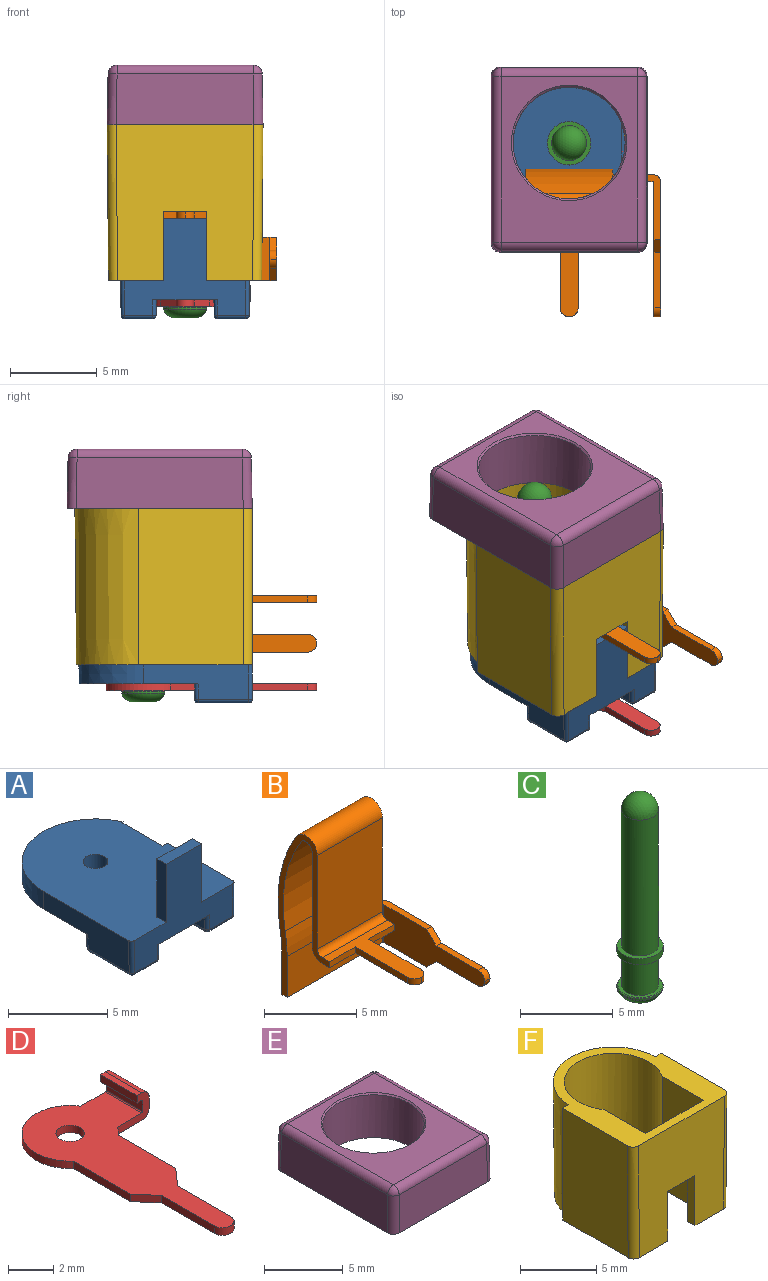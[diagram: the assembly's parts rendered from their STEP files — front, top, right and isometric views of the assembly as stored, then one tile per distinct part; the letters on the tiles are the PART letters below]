
ASSEMBLY  parts=6 mates=5
PART A: 44 faces, bbox 7.4x10x5.8 mm
  f0: cylinder r=0.62mm len=1.25mm, axis (0,0,1), area 4.3mm2, adj f1,f2
  f1: plane 9.98x7.4mm, normal (0,0,-1), area 52.3mm2, adj f0,f3,f4,f5,f6,f7,f8,f9
  f2: plane 9.99x7.41mm, normal (0,0,1), area 64.3mm2, adj f0,f3,f4,f5,f6,f7,f8,f9
  f3: plane 4.63x1.99mm, normal (1,0,-0.01), area 7.7mm2, adj f1,f2,f9,f34,f39,f40
  f4: plane 7.01x5.58mm, normal (0,-1,0), area 19.5mm2, adj f1,f2,f10,f11,f12,f25,f28,f31
  f5: plane 6.08x1.99mm, normal (-1,0,-0.01), area 9.3mm2, adj f1,f2,f6,f22,f27,f28
  f6: cone r=3.79mm half-angle=0.5deg, axis (0,0,1), area 11.1mm2, adj f1,f2,f5,f7
  f7: plane 1.09x0.08mm, normal (0,-1,0), area 0.1mm2, adj f1,f2,f6,f8
  f8: plane 2.9x1.09mm, normal (1,0,0), area 3.2mm2, adj f1,f2,f7,f9
  f9: plane 1.09x0.37mm, normal (0,1,0), area 0.4mm2, adj f1,f2,f3,f8
  f10: plane 3.59x0.65mm, normal (-1,0,0), area 2.3mm2, adj f2,f4,f11,f13
  f11: plane 2.5x0.65mm, normal (0,0,1), area 1.6mm2, adj f4,f10,f12,f13
  f12: plane 3.59x0.65mm, normal (1,0,0), area 2.3mm2, adj f2,f4,f11,f13
  f13: plane 3.59x2.5mm, normal (0,1,0), area 9mm2, adj f2,f10,f11,f12
  f14: plane 2.92x0.9mm, normal (-1,0,-0.01), area 2.6mm2, adj f1,f32,f37,f38
  f15: plane 1.63x0.9mm, normal (0,1,-0.01), area 1.5mm2, adj f1,f37,f40,f43
  f16: plane 2.91x1.62mm, normal (0,0,-1), area 4.7mm2, adj f33,f38,f39,f43
  f17: plane 1.63x0.9mm, normal (0,1,-0.01), area 1.5mm2, adj f1,f20,f21,f22
  f18: plane 2.92x0.9mm, normal (1,0,-0.01), area 2.6mm2, adj f1,f20,f25,f26
  f19: plane 2.91x1.62mm, normal (0,0,-1), area 4.7mm2, adj f21,f26,f27,f31
  f20: cylinder r=0.2mm len=0.9mm, axis (0.01,0.01,1), area 0.3mm2, adj f1,f17,f18,f23
  f21: cylinder r=0.2mm len=1.62mm, axis (1,0,0), area 0.5mm2, adj f17,f19,f23,f24
  f22: cylinder r=0.2mm len=0.9mm, axis (-0.01,0.01,1), area 0.3mm2, adj f1,f5,f17,f24
  f23: sphere r=0.2mm, area 0.1mm2, adj f20,f21,f26
  f24: sphere r=0.2mm, area 0.1mm2, adj f21,f22,f27
  f25: cylinder r=0.2mm len=0.9mm, axis (-0.01,0,-1), area 0.3mm2, adj f1,f4,f18,f29
  f26: cylinder r=0.2mm len=2.91mm, axis (0,-1,0), area 0.9mm2, adj f18,f19,f23,f29
  f27: cylinder r=0.2mm len=2.91mm, axis (0,1,0), area 0.9mm2, adj f5,f19,f24,f30
  f28: cylinder r=0.2mm len=1.99mm, axis (0.01,0,-1), area 0.6mm2, adj f2,f4,f5,f30
  f29: sphere r=0.2mm, area 0.1mm2, adj f25,f26,f31
  f30: sphere r=0.2mm, area 0.1mm2, adj f27,f28,f31
  f31: cylinder r=0.2mm len=1.62mm, axis (1,0,0), area 0.5mm2, adj f4,f19,f29,f30
  f32: cylinder r=0.2mm len=0.9mm, axis (0.01,0,-1), area 0.3mm2, adj f1,f4,f14,f35
  f33: cylinder r=0.2mm len=1.62mm, axis (-1,0,0), area 0.5mm2, adj f4,f16,f35,f36
  f34: cylinder r=0.2mm len=1.99mm, axis (-0.01,0,-1), area 0.6mm2, adj f2,f3,f4,f36
  f35: sphere r=0.2mm, area 0.1mm2, adj f32,f33,f38
  f36: sphere r=0.2mm, area 0.1mm2, adj f33,f34,f39
  f37: cylinder r=0.2mm len=0.9mm, axis (-0.01,0.01,1), area 0.3mm2, adj f1,f14,f15,f41
  f38: cylinder r=0.2mm len=2.91mm, axis (0,-1,0), area 0.9mm2, adj f14,f16,f35,f41
  f39: cylinder r=0.2mm len=2.91mm, axis (0,1,0), area 0.9mm2, adj f3,f16,f36,f42
  f40: cylinder r=0.2mm len=0.9mm, axis (0.01,0.01,1), area 0.3mm2, adj f1,f3,f15,f42
  f41: sphere r=0.2mm, area 0.1mm2, adj f37,f38,f43
  f42: sphere r=0.2mm, area 0.1mm2, adj f39,f40,f43
  f43: cylinder r=0.2mm len=1.62mm, axis (-1,0,0), area 0.5mm2, adj f15,f16,f41,f42
PART B: 34 faces, bbox 7.8x8.5x11.5 mm
  f0: plane 1.99x0.4mm, normal (0,-1,0), area 0.8mm2, adj f15,f17,f18,f30
  f1: plane 3.74x2.78mm, normal (0,0,1), area 2.4mm2, adj f4,f5,f6,f7,f8,f9,f11,f18
  f2: plane 3.21x0.4mm, normal (0,0,1), area 1.3mm2, adj f8,f9,f11,f14
  f3: plane 3.21x0.4mm, normal (0,0,-1), area 1.3mm2, adj f8,f9,f12,f13
  f4: plane 7.33x2.74mm, normal (0,1,0), area 19.5mm2, adj f1,f6,f10,f16,f18,f27
  f5: plane 7.33x2.74mm, normal (0,-1,0), area 19.5mm2, adj f1,f7,f10,f16,f18,f28
  f6: cylinder r=0.45mm len=2.5mm, axis (0,0,1), area 1.8mm2, adj f1,f4,f9,f10
  f7: cylinder r=0.05mm len=2.5mm, axis (0,0,1), area 0.2mm2, adj f1,f5,f8,f10
  f8: plane 7.75x2.5mm, normal (-1,0,0), area 13.2mm2, adj f1,f2,f3,f7,f10,f11,f12,f13
  f9: plane 7.75x2.5mm, normal (1,0,0), area 13.2mm2, adj f1,f2,f3,f6,f10,f11,f12,f13
  f10: plane 7.78x3.74mm, normal (0,0,-1), area 4.4mm2, adj f4,f5,f6,f7,f8,f9,f12,f16
  f11: plane 0.74x0.74mm, normal (0,-0.71,0.71), area 0.4mm2, adj f1,f2,f8,f9
  f12: plane 0.74x0.74mm, normal (0,-0.71,-0.71), area 0.4mm2, adj f3,f8,f9,f10
  f13: cylinder r=0.52mm len=0.52mm, axis (-1,0,0), area 0.3mm2, adj f3,f8,f9,f14
  f14: cylinder r=0.52mm len=0.52mm, axis (1,0,0), area 0.3mm2, adj f2,f8,f9,f13
  f15: plane 5.1x5mm, normal (0,0,1), area 7.3mm2, adj f0,f16,f18,f19,f29,f30,f31,f32
  f16: plane 11.48x3.96mm, normal (-1,0,0), area 8.3mm2, adj f4,f5,f10,f15,f17,f19,f20,f21
  f17: plane 5.1x5mm, normal (0,0,-1), area 7.3mm2, adj f0,f16,f18,f20,f29,f30,f31,f32
  f18: plane 8.98x3.96mm, normal (1,0,0), area 7.3mm2, adj f0,f1,f4,f5,f15,f17,f19,f20
  f19: cylinder r=0.38mm len=5mm, axis (-1,0,0), area 3mm2, adj f15,f16,f18,f21
  f20: cylinder r=0.78mm len=5mm, axis (-1,0,0), area 6.1mm2, adj f16,f17,f18,f22
  f21: plane 6.24x5mm, normal (0,-1,0), area 31.2mm2, adj f16,f18,f19,f23
  f22: plane 6.24x5mm, normal (0,1,0), area 31.2mm2, adj f16,f18,f20,f24
  f23: cylinder r=0.87mm len=5mm, axis (1,0,0), area 11.3mm2, adj f16,f18,f21,f25
  f24: cylinder r=0.47mm len=5mm, axis (1,0,0), area 6.1mm2, adj f16,f18,f22,f26
  f25: cylinder r=9.54mm len=6.81mm, axis (1,0,0), area 35.4mm2, adj f16,f18,f23,f27
  f26: cylinder r=9.14mm len=6.52mm, axis (1,0,0), area 33.9mm2, adj f16,f18,f24,f28
  f27: cylinder r=8.08mm len=5mm, axis (-1,0,0), area 7.7mm2, adj f4,f16,f18,f25
  f28: cylinder r=8.48mm len=5mm, axis (-1,0,0), area 8mm2, adj f5,f16,f18,f26
  f29: plane 1.99x0.4mm, normal (0,-1,0), area 0.8mm2, adj f15,f16,f17,f31
  f30: plane 4.04x0.4mm, normal (1,0,0), area 1.6mm2, adj f0,f15,f17,f32
  f31: plane 4.04x0.4mm, normal (-1,0,0), area 1.6mm2, adj f15,f17,f29,f33
  f32: cylinder r=0.52mm len=0.52mm, axis (0,0,-1), area 0.3mm2, adj f15,f17,f30,f33
  f33: cylinder r=0.52mm len=0.52mm, axis (0,0,1), area 0.3mm2, adj f15,f17,f31,f32
PART C: 14 faces, bbox 2.7x2.7x13.2 mm
  f0: cylinder r=1.25mm len=2.5mm, axis (0,0,-1), area 0.7mm2, adj f1,f9
  f1: torus R=1.2mm, axis (0,0,-1), area 0.1mm2, adj f0,f2
  f2: torus R=0.54mm, axis (0,0,-1), area 5mm2, adj f1,f3
  f3: torus R=0.66mm, axis (0,0,-1), area 0.3mm2, adj f2,f4
  f4: cylinder r=0.61mm len=1.3mm, axis (0,0,-1), area 5mm2, adj f3,f13
  f5: sphere r=1mm, area 6.3mm2, adj f6
  f6: cylinder r=1mm len=8.98mm, axis (0,0,-1), area 56.4mm2, adj f5,f12
  f7: cylinder r=1.25mm len=2.5mm, axis (0,0,-1), area 3.1mm2, adj f11,f12
  f8: cylinder r=1mm len=2.21mm, axis (0,0,-1), area 13.9mm2, adj f10,f11
  f9: torus R=1.2mm, axis (0,0,-1), area 0.6mm2, adj f0,f10
  f10: plane 2.4x2.4mm, normal (0,0,1), area 1.4mm2, adj f8,f9
  f11: plane 2.5x2.5mm, normal (0,0,-1), area 1.8mm2, adj f7,f8
  f12: plane 2.5x2.5mm, normal (0,0,1), area 1.8mm2, adj f6,f7
  f13: plane 1.22x1.22mm, normal (0,0,-1), area 1.2mm2, adj f4
PART D: 23 faces, bbox 5.9x12.1x1.5 mm
  f0: cylinder r=0.62mm len=1.25mm, axis (0,0,1), area 1.6mm2, adj f3,f4
  f1: cylinder r=2.12mm len=3.92mm, axis (0,0,1), area 2.9mm2, adj f3,f4,f11,f12
  f2: cylinder r=2.12mm len=0.46mm, axis (0,0,1), area 0.2mm2, adj f3,f4,f5,f13
  f3: plane 12.13x5.46mm, normal (0,0,-1), area 30.7mm2, adj f0,f1,f2,f5,f6,f7,f8,f9
  f4: plane 12.13x5.46mm, normal (0,0,1), area 30.7mm2, adj f0,f1,f2,f5,f6,f7,f8,f9
  f5: plane 3.58x0.4mm, normal (1,0,0), area 1.4mm2, adj f2,f3,f4,f6
  f6: plane 1x0.89mm, normal (0.75,-0.66,0), area 0.5mm2, adj f3,f4,f5,f7
  f7: plane 3.31x0.4mm, normal (1,0,0), area 1.3mm2, adj f3,f4,f6,f8
  f8: cylinder r=0.52mm len=1.03mm, axis (0,0,1), area 0.6mm2, adj f3,f4,f7,f9
  f9: plane 3.31x0.4mm, normal (-1,0,0), area 1.3mm2, adj f3,f4,f8,f10
  f10: plane 1x0.89mm, normal (-0.75,-0.66,0), area 0.5mm2, adj f3,f4,f9,f11
  f11: plane 3.58x0.4mm, normal (-1,0,0), area 1.4mm2, adj f1,f3,f4,f10
  f12: plane 1.99x1.49mm, normal (0,1,0), area 1.3mm2, adj f1,f3,f4,f14,f15,f16,f17,f18
  f13: plane 1.99x1.49mm, normal (0,-1,0), area 1.3mm2, adj f2,f3,f4,f14,f15,f16,f17,f18
  f14: plane 2.28x0.3mm, normal (0,0,-1), area 0.7mm2, adj f12,f13,f16,f22
  f15: plane 2.28x0.3mm, normal (0,0,1), area 0.7mm2, adj f12,f13,f17,f22
  f16: cylinder r=0.05mm len=2.28mm, axis (0,-1,0), area 0.2mm2, adj f12,f13,f14,f18
  f17: cylinder r=0.45mm len=2.28mm, axis (0,-1,0), area 1.6mm2, adj f12,f13,f15,f19
  f18: plane 2.28x0.59mm, normal (-1,0,0), area 1.3mm2, adj f12,f13,f16,f20
  f19: plane 2.28x0.59mm, normal (1,0,0), area 1.3mm2, adj f12,f13,f17,f21
  f20: cylinder r=0.05mm len=2.28mm, axis (0,-1,0), area 0.2mm2, adj f4,f12,f13,f18
  f21: cylinder r=0.45mm len=2.28mm, axis (0,-1,0), area 1.6mm2, adj f3,f12,f13,f19
  f22: plane 2.28x0.4mm, normal (-1,0,0), area 0.9mm2, adj f12,f13,f14,f15
PART E: 24 faces, bbox 9x10.7x3.4 mm
  f0: cone r=3.23mm half-angle=45deg, axis (0,0,1), area 2.9mm2, adj f1,f6
  f1: cylinder r=3.23mm len=6.45mm, axis (0,0,-1), area 50mm2, adj f0,f7,f8,f9,f11
  f2: plane 9.62x2.92mm, normal (1,0,0.02), area 27.9mm2, adj f7,f14,f19,f20
  f3: plane 7.94x2.92mm, normal (0,1,0.02), area 23mm2, adj f7,f12,f13,f14
  f4: plane 9.62x2.92mm, normal (-1,0,0.02), area 27.9mm2, adj f7,f12,f17,f18
  f5: plane 7.94x2.92mm, normal (0,-1,0.02), area 23mm2, adj f7,f17,f20,f23
  f6: plane 9.52x7.84mm, normal (0,0,1), area 39.9mm2, adj f0,f13,f18,f19,f23
  f7: plane 10.67x8.99mm, normal (0,0,-1), area 47.8mm2, adj f1,f2,f3,f4,f5,f9,f10,f11
  f8: plane 5.33x3.81mm, normal (0,0,-1), area 15.1mm2, adj f1,f9,f10,f11
  f9: plane 3.81x2.78mm, normal (-1,0,0), area 10.6mm2, adj f1,f7,f8,f10
  f10: plane 5.33x2.78mm, normal (0,1,0), area 14.8mm2, adj f7,f8,f9,f11
  f11: plane 3.81x2.78mm, normal (1,0,0), area 10.6mm2, adj f1,f7,f8,f10
  f12: cylinder r=0.52mm len=2.92mm, axis (-0.02,0.02,-1), area 2.4mm2, adj f3,f4,f7,f15
  f13: cylinder r=0.52mm len=7.84mm, axis (1,0,0), area 6.3mm2, adj f3,f6,f15,f16
  f14: cylinder r=0.52mm len=2.92mm, axis (0.02,0.02,-1), area 2.4mm2, adj f2,f3,f7,f16
  f15: sphere r=0.52mm, area 0.4mm2, adj f12,f13,f18
  f16: sphere r=0.52mm, area 0.4mm2, adj f13,f14,f19
  f17: cylinder r=0.52mm len=2.92mm, axis (-0.02,-0.02,-1), area 2.4mm2, adj f4,f5,f7,f21
  f18: cylinder r=0.52mm len=9.52mm, axis (0,-1,0), area 7.7mm2, adj f4,f6,f15,f21
  f19: cylinder r=0.52mm len=9.52mm, axis (0,-1,0), area 7.7mm2, adj f2,f6,f16,f22
  f20: cylinder r=0.52mm len=2.92mm, axis (0.02,-0.02,-1), area 2.4mm2, adj f2,f5,f7,f22
  f21: sphere r=0.52mm, area 0.4mm2, adj f17,f18,f23
  f22: sphere r=0.52mm, area 0.4mm2, adj f19,f20,f23
  f23: cylinder r=0.52mm len=7.84mm, axis (1,0,0), area 6.3mm2, adj f5,f6,f21,f22
PART F: 21 faces, bbox 9x10.2x9 mm
  f0: cylinder r=3.23mm len=9mm, axis (0,0,1), area 125.9mm2, adj f2,f3,f10,f11,f17,f18
  f1: plane 4.08x3.16mm, normal (0,0,-1), area 8mm2, adj f6,f7,f11,f12,f13,f16,f20
  f2: plane 10.14x8.82mm, normal (0,0,-1), area 20.9mm2, adj f0,f4,f5,f6,f7,f8,f9,f10
  f3: plane 10.22x8.98mm, normal (0,0,1), area 33.1mm2, adj f0,f4,f5,f6,f7,f8,f9,f10
  f4: cone r=3.94mm half-angle=0.5deg, axis (0,0,1), area 107.2mm2, adj f2,f3,f5,f9
  f5: plane 9x0.63mm, normal (0,1,0), area 5mm2, adj f2,f3,f4,f6
  f6: plane 9x5.83mm, normal (1,0,-0.01), area 51.5mm2, adj f1,f2,f3,f5,f16,f17,f18,f20
  f7: plane 9x7.94mm, normal (0,-1,0), area 60.8mm2, adj f1,f2,f3,f13,f14,f15,f19,f20
  f8: plane 9x6.03mm, normal (-1,0,-0.01), area 54.3mm2, adj f2,f3,f9,f19
  f9: plane 9x0.64mm, normal (0,1,0), area 5mm2, adj f2,f3,f4,f8
  f10: plane 9x3.81mm, normal (1,0,0), area 34.3mm2, adj f0,f2,f3,f12
  f11: plane 9x3.81mm, normal (-1,0,0), area 33.4mm2, adj f0,f1,f3,f12,f16,f18
  f12: plane 9x5.33mm, normal (0,1,0), area 38mm2, adj f1,f2,f3,f10,f11,f13,f14,f15
  f13: plane 3.99x0.65mm, normal (-1,0,0), area 2.6mm2, adj f1,f7,f12,f14
  f14: plane 2.5x0.65mm, normal (0,0,-1), area 1.6mm2, adj f7,f12,f13,f15
  f15: plane 3.99x0.65mm, normal (1,0,0), area 2.6mm2, adj f2,f7,f12,f14
  f16: plane 2.5x1.77mm, normal (0,1,0), area 4.4mm2, adj f1,f6,f11,f18
  f17: plane 2.5x1.76mm, normal (0,-1,0), area 4.4mm2, adj f0,f2,f6,f18
  f18: plane 1.77x0.4mm, normal (0,0,-1), area 0.7mm2, adj f0,f6,f11,f16,f17
  f19: cylinder r=0.52mm len=9.01mm, axis (0.01,0,-1), area 7.4mm2, adj f2,f3,f7,f8
  f20: cylinder r=0.52mm len=9.01mm, axis (-0.01,0,-1), area 7.4mm2, adj f1,f3,f6,f7
PLACE A at identity
PLACE B t=(0.01,-0.01,0)mm
PLACE C t=(0,0,0.01)mm
PLACE D at identity
PLACE E at identity fixed
PLACE F at identity
MATE fastened D.f0 <-> A.f0  axis (0,0,1) through (0,0,-10.09)mm
MATE fastened D.f8 <-> B.f32  axis (0,0,1) through (0,-9.49,-10.09)mm
MATE fastened F.f0 <-> A.f0  axis (0,0,-1) through (0,0,-9)mm
MATE fastened E.f7 <-> F.f3  axis (0,0,-1) through (3.97,-5.76,0)mm
MATE fastened D.f0 <-> C.f0  axis (0,0,-1) through (0,0,-10.49)mm
